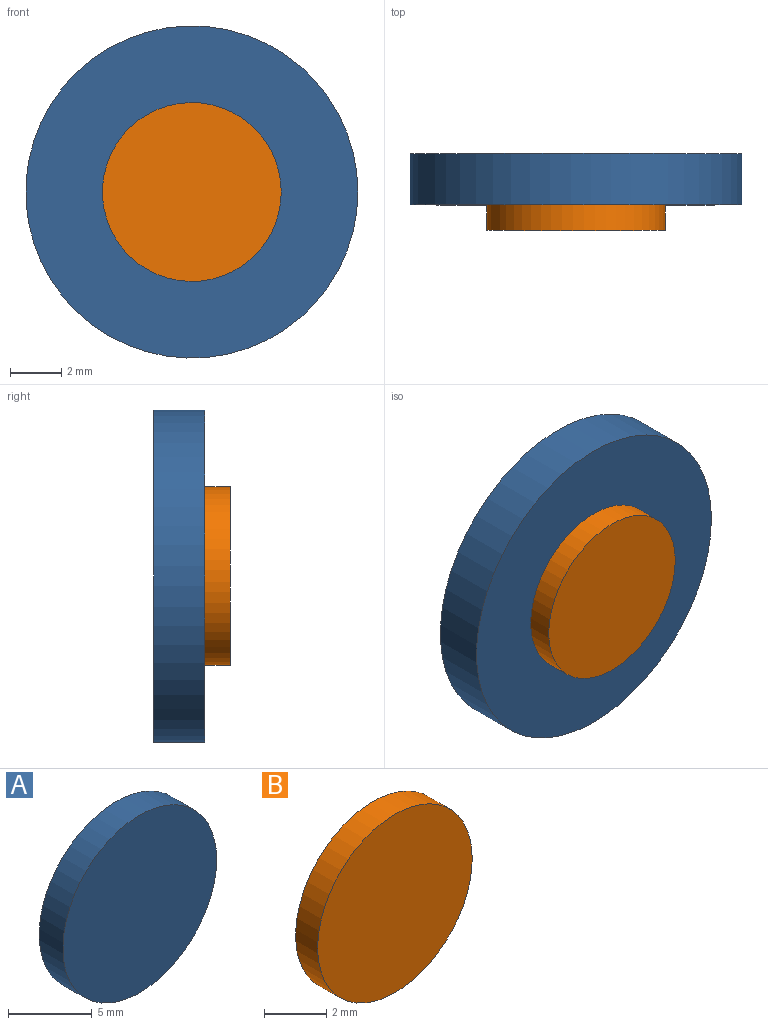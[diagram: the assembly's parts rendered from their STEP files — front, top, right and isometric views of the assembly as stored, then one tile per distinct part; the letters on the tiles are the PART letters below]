
ASSEMBLY  parts=2 mates=1
PART A: 3 faces, bbox 13x2x13 mm
  f0: cylinder r=6.5mm len=13mm, axis (0,-1,0), area 81.7mm2, adj f1,f2
  f1: plane 13x13mm, normal (0,1,0), area 132.7mm2, adj f0
  f2: plane 13x13mm, normal (0,-1,0), area 132.7mm2, adj f0
PART B: 3 faces, bbox 7x1x7 mm
  f0: cylinder r=3.5mm len=7mm, axis (0,1,0), area 22mm2, adj f1,f2
  f1: plane 7x7mm, normal (0,-1,0), area 38.5mm2, adj f0
  f2: plane 7x7mm, normal (0,1,0), area 38.5mm2, adj f0
PLACE A at identity
PLACE B at identity
MATE fastened B.f0 <-> A.f0  axis (0,1,0) through (0,0,0)mm
